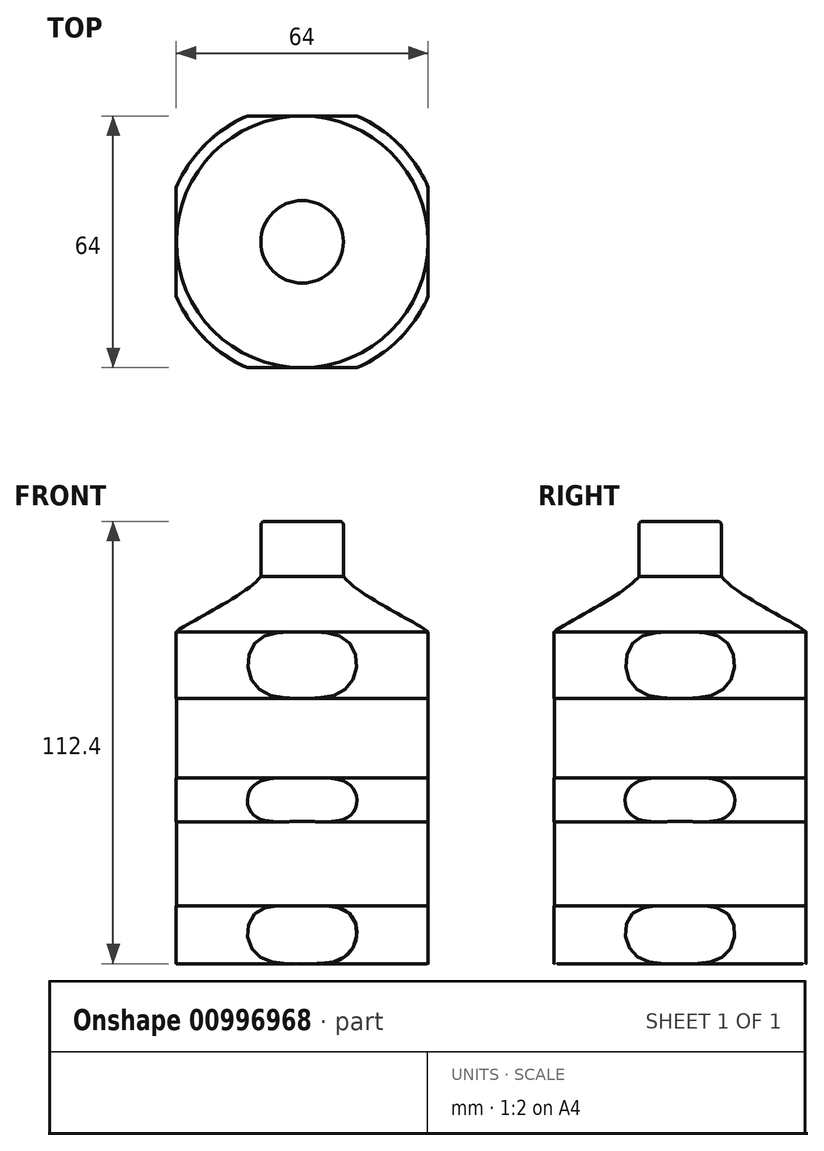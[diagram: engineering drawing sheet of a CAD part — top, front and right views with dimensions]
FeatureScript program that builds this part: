
annotation { "Feature Type Name" : "Feature", "Feature Type Description" : "" }
export const myFeature = defineFeature(function(context is Context, id is Id, definition is map)
    precondition{}
    {
        {
            var Q0;
            Q0=qCreatedBy(makeId("Front.planeOp"),FACE);
            var sketch = newSketch(context, id + "F0", { "sketchPlane" : qUnion([Q0])});
            skFitSpline(sketch, "E0", {"points": [v(-31.96, 0) * mm, v(-31.96, 14.73) * mm], "startDerivative": vector(-10.5, 0) * mm, "endDerivative": vector(12.87, -0.63) * mm});
            skLineSegment(sketch, "E1", {"start": v(-31.96, 14.73) * mm, "end": v(-31.96, 36.13) * mm});
            skFitSpline(sketch, "E2", {"points": [v(-31.96, 36.13) * mm, v(-31.96, 47.17) * mm], "startDerivative": vector(-11.77, -3.42) * mm, "endDerivative": vector(11.77, -1.85) * mm});
            skLineSegment(sketch, "E3", {"start": v(-31.96, 47.17) * mm, "end": v(-31.96, 67.4) * mm});
            skFitSpline(sketch, "E4", {"points": [v(-31.96, 67.4) * mm, v(-31.96, 84.32) * mm], "startDerivative": vector(-11.58, 4.36) * mm, "endDerivative": vector(11.59, 1.81) * mm});
            skFitSpline(sketch, "E5", {"points": [v(-31.96, 84.32) * mm, v(-10.49, 98.35) * mm], "startDerivative": vector(4.62, 5.17) * mm, "endDerivative": vector(11.2, 14.57) * mm});
            skLineSegment(sketch, "E6", {"start": v(-10.49, 98.35) * mm, "end": v(-10.49, 112.4) * mm});
            skLineSegment(sketch, "E7", {"start": v(-10.49, 112.4) * mm, "end": v(0, 112.4) * mm});
            skLineSegment(sketch, "E8", {"start": v(0, 0) * mm, "end": v(0, 112.4) * mm});
            skLineSegment(sketch, "E9", {"start": v(-31.03, 96.24) * mm, "end": v(-35.82, -1488.31) * mm, "construction": true});
            skLineSegment(sketch, "E10", {"start": v(0, 0) * mm, "end": v(-31.96, 0) * mm});
            skSolve(sketch);
        }
        {
            var Q0;
            Q0 = qSketchRegion(id + "F0", true);
            var Q1;
            Q1=sQuery(id+"F0.wireOp",EDGE,"E8");
            revolve(context, id + "F1", {"surfaceOperationType" : NewSurfaceOperationType.NEW, "entities" : qUnion([Q0]), "axis" : qUnion([Q1]), "revolveType" : RevolveType.FULL});
        }
        {
            var Q0;
            Q0=makeQuery(id+"F1.opRevolve","SWEPT_EDGE",EDGE,{"disambiguationData":[OSD([sQuery(id+"F0.wireOp",EDGE,"E6"),sQuery(id+"F0.wireOp",EDGE,"E7")])]});
            fillet(context, id + "F2", {"entities" : qUnion([Q0]), "radius" : 1 * mm, "tangentPropagation" : true, "allowEdgeOverflow" : false});
        }
        {
            var Q0;
            Q0=qCreatedBy(makeId("Right.planeOp"),FACE);
            var sketch = newSketch(context, id + "F3", { "sketchPlane" : qUnion([Q0])});
            skLineSegment(sketch, "E11.bottom", {"start": v(-32, -5.7) * mm, "end": v(-46.25, -5.7) * mm});
            skLineSegment(sketch, "E11.top", {"start": v(-32, 85.93) * mm, "end": v(-46.25, 85.93) * mm});
            skLineSegment(sketch, "E11.left", {"start": v(-32, -5.7) * mm, "end": v(-32, 85.93) * mm});
            skLineSegment(sketch, "E11.right", {"start": v(-46.25, -5.7) * mm, "end": v(-46.25, 85.93) * mm});
            skSolve(sketch);
        }
        {
            var Q0;
            Q0 = qSketchRegion(id + "F3", true);
            extrude(context, id + "F4", {"entities" : qUnion([Q0]), "operationType" : NewBodyOperationType.REMOVE, "endBound" : BoundingType.SYMMETRIC, "depth" : 50 * mm, "offsetDistance" : 25 * mm});
        }
        {
            var Q0;
            Q0=qCreatedBy(makeId("Right.planeOp"),FACE);
            var sketch = newSketch(context, id + "F5", { "sketchPlane" : qUnion([Q0])});
            skLineSegment(sketch, "E12.bottom", {"start": v(32, -2.2) * mm, "end": v(53.41, -2.2) * mm});
            skLineSegment(sketch, "E12.top", {"start": v(32, 88.68) * mm, "end": v(53.41, 88.68) * mm});
            skLineSegment(sketch, "E12.left", {"start": v(32, -2.2) * mm, "end": v(32, 88.68) * mm});
            skLineSegment(sketch, "E12.right", {"start": v(53.41, -2.2) * mm, "end": v(53.41, 88.68) * mm});
            skSolve(sketch);
        }
        {
            var Q0;
            Q0 = qSketchRegion(id + "F5", true);
            extrude(context, id + "F6", {"entities" : qUnion([Q0]), "operationType" : NewBodyOperationType.REMOVE, "endBound" : BoundingType.SYMMETRIC, "oppositeDirection" : true, "depth" : 50 * mm, "offsetDistance" : 25 * mm});
        }
        {
            var Q0;
            Q0=qCreatedBy(makeId("Front.planeOp"),FACE);
            var sketch = newSketch(context, id + "F7", { "sketchPlane" : qUnion([Q0])});
            skLineSegment(sketch, "E13.bottom", {"start": v(-32, -9.9) * mm, "end": v(-53.65, -9.9) * mm});
            skLineSegment(sketch, "E13.top", {"start": v(-32, 90.26) * mm, "end": v(-53.65, 90.26) * mm});
            skLineSegment(sketch, "E13.left", {"start": v(-32, -9.9) * mm, "end": v(-32, 90.26) * mm});
            skLineSegment(sketch, "E13.right", {"start": v(-53.65, -9.9) * mm, "end": v(-53.65, 90.26) * mm});
            skSolve(sketch);
        }
        {
            var Q0;
            Q0 = qSketchRegion(id + "F7", true);
            extrude(context, id + "F8", {"entities" : qUnion([Q0]), "operationType" : NewBodyOperationType.REMOVE, "endBound" : BoundingType.SYMMETRIC, "depth" : 50 * mm, "offsetDistance" : 25 * mm});
        }
        {
            var Q0;
            Q0=qCreatedBy(makeId("Front.planeOp"),FACE);
            var sketch = newSketch(context, id + "F9", { "sketchPlane" : qUnion([Q0])});
            skLineSegment(sketch, "E14.bottom", {"start": v(32, -2.9) * mm, "end": v(52.16, -2.9) * mm});
            skLineSegment(sketch, "E14.top", {"start": v(32, 92.29) * mm, "end": v(52.16, 92.29) * mm});
            skLineSegment(sketch, "E14.left", {"start": v(32, -2.9) * mm, "end": v(32, 92.29) * mm});
            skLineSegment(sketch, "E14.right", {"start": v(52.16, -2.9) * mm, "end": v(52.16, 92.29) * mm});
            skSolve(sketch);
        }
        {
            var Q0;
            Q0 = qSketchRegion(id + "F9", true);
            extrude(context, id + "F10", {"entities" : qUnion([Q0]), "operationType" : NewBodyOperationType.REMOVE, "endBound" : BoundingType.SYMMETRIC, "depth" : 50 * mm, "offsetDistance" : 25 * mm});
        }
    });
